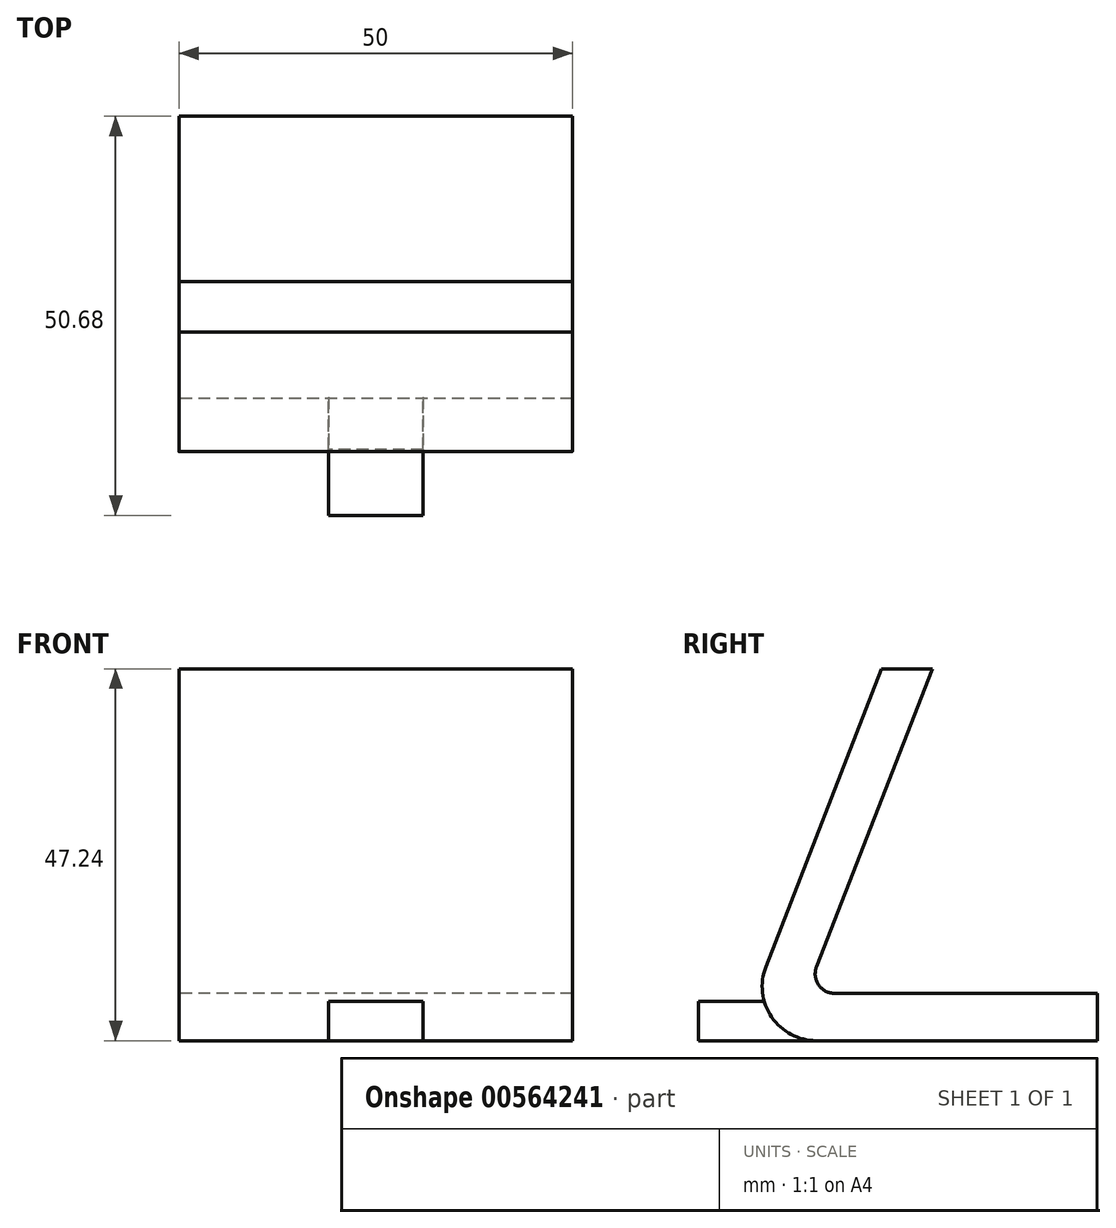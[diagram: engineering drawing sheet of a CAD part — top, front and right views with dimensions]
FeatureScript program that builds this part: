
annotation { "Feature Type Name" : "Feature", "Feature Type Description" : "" }
export const myFeature = defineFeature(function(context is Context, id is Id, definition is map)
    precondition{}
    {
        {
            var Q0;
            Q0=qCreatedBy(makeId("Right.planeOp"),FACE);
            var sketch = newSketch(context, id + "F0", { "sketchPlane" : qUnion([Q0])});
            skLineSegment(sketch, "E0", {"start": v(43, 0) * mm, "end": v(7.32, 0) * mm});
            skLineSegment(sketch, "E1", {"start": v(0.89, 9.4) * mm, "end": v(15.58, 47.24) * mm});
            skLineSegment(sketch, "E2", {"start": v(22.02, 47.24) * mm, "end": v(7.32, 9.4) * mm});
            skLineSegment(sketch, "E3", {"start": v(9.65, 6) * mm, "end": v(43, 6) * mm});
            skLineSegment(sketch, "E4", {"start": v(43, 6) * mm, "end": v(43, 0) * mm});
            skPoint(sketch, "E5.visualSharp", {"position": v(6, 6) * mm});
            skArc(sketch, "E5.filletArc", {"start": v(7.32, 9.4) * mm, "mid": v(7.59, 7.09) * mm, "end": v(9.65, 6) * mm});
            skPoint(sketch, "E6.visualSharp", {"position": v(0, 0) * mm});
            skLineSegment(sketch, "E7", {"start": v(15.58, 47.24) * mm, "end": v(22.02, 47.24) * mm});
            skArc(sketch, "E8", {"start": v(0.89, 9.4) * mm, "mid": v(1.62, 3) * mm, "end": v(7.32, 0) * mm});
            skSolve(sketch);
        }
        {
            var Q0;
            Q0 = qSketchRegion(id + "F0", true);
            extrude(context, id + "F1", {"entities" : qUnion([Q0]), "endBound" : BoundingType.SYMMETRIC, "depth" : 50 * mm, "offsetDistance" : 25 * mm});
        }
        {
            var Q0;
            Q0=makeQuery(id+"F1.opExtrude","SWEPT_FACE",FACE,{"disambiguationData":[OSD([sQuery(id+"F0.wireOp",EDGE,"E3")])]});
            var sketch = newSketch(context, id + "F2", { "sketchPlane" : qUnion([Q0])});
            skLineSegment(sketch, "E9.0", {"start": v(25, 9.65) * mm, "end": v(25, 43) * mm, "construction": true});
            skLineSegment(sketch, "E10.0", {"start": v(25, 9.65) * mm, "end": v(-25, 9.65) * mm, "construction": true});
            skLineSegment(sketch, "E11.0", {"start": v(-25, 9.65) * mm, "end": v(-25, 43) * mm, "construction": true});
            skLineSegment(sketch, "E12.0", {"start": v(25, 43) * mm, "end": v(-25, 43) * mm, "construction": true});
            skLineSegment(sketch, "E13.bottom", {"start": v(20, 43) * mm, "end": v(-20, 43) * mm});
            skLineSegment(sketch, "E13.top", {"start": v(20, 9.65) * mm, "end": v(-20, 9.65) * mm});
            skLineSegment(sketch, "E13.left", {"start": v(20, 43) * mm, "end": v(20, 9.65) * mm});
            skLineSegment(sketch, "E13.right", {"start": v(-20, 43) * mm, "end": v(-20, 9.65) * mm});
            skSolve(sketch);
        }
        {
            var Q0;
            Q0=qCreatedBy(makeId("Top.planeOp"),FACE);
            var sketch = newSketch(context, id + "F3", { "sketchPlane" : qUnion([Q0])});
            skPoint(sketch, "E14.0", {"position": v(0, 7.32) * mm});
            skLineSegment(sketch, "E15.bottom", {"start": v(-6, 7.32) * mm, "end": v(6, 7.32) * mm});
            skLineSegment(sketch, "E15.top", {"start": v(-6, -7.68) * mm, "end": v(6, -7.68) * mm});
            skLineSegment(sketch, "E15.left", {"start": v(-6, 7.32) * mm, "end": v(-6, -7.68) * mm});
            skLineSegment(sketch, "E15.right", {"start": v(6, 7.32) * mm, "end": v(6, -7.68) * mm});
            skSolve(sketch);
        }
        {
            var Q0;
            Q0 = qSketchRegion(id + "F3", true);
            extrude(context, id + "F4", {"entities" : qUnion([Q0]), "operationType" : NewBodyOperationType.ADD, "depth" : 5 * mm, "offsetDistance" : 25 * mm});
        }
    });
